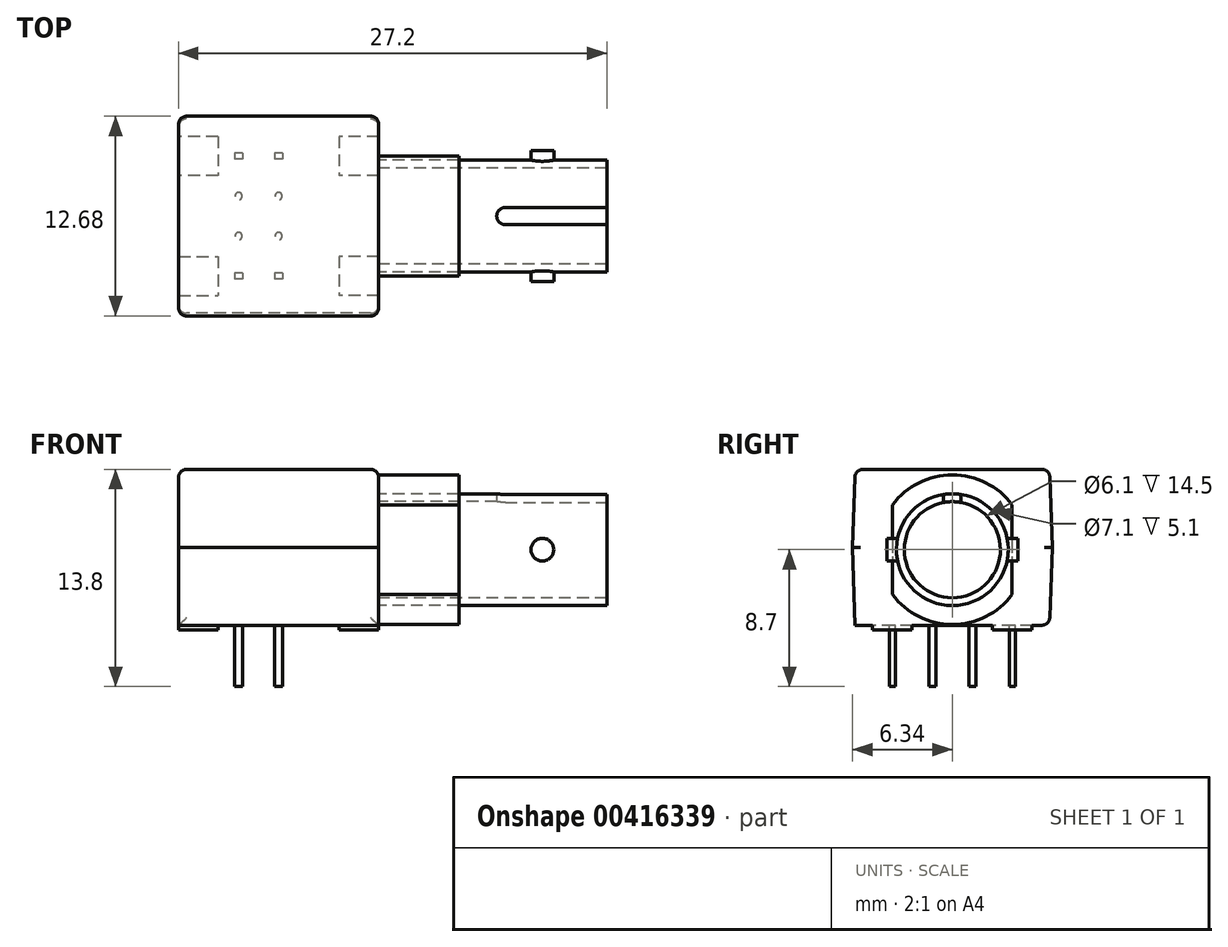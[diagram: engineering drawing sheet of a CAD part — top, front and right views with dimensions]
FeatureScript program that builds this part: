
annotation { "Feature Type Name" : "Feature", "Feature Type Description" : "" }
export const myFeature = defineFeature(function(context is Context, id is Id, definition is map)
    precondition{}
    {
        {
            var Q0;
            Q0=qCreatedBy(makeId("Top.planeOp"),FACE);
            var sketch = newSketch(context, id + "F0", { "sketchPlane" : qUnion([Q0])});
            skLineSegment(sketch, "E0.bottom", {"start": v(-6.35, 6.35) * mm, "end": v(6.35, 6.35) * mm});
            skLineSegment(sketch, "E0.top", {"start": v(-6.35, -6.35) * mm, "end": v(6.35, -6.35) * mm});
            skLineSegment(sketch, "E0.left", {"start": v(-6.35, 6.35) * mm, "end": v(-6.35, -6.35) * mm});
            skLineSegment(sketch, "E0.right", {"start": v(6.35, 6.35) * mm, "end": v(6.35, -6.35) * mm});
            skPoint(sketch, "E0.middle", {"position": v(0, 0) * mm});
            skSolve(sketch);
        }
        {
            var Q0;
            Q0=makeQuery(id+"F0.imprint","IMPRINT",FACE,{"disambiguationData":[TD([[makeQuery(id+"F0.imprint","IMPRINT",EDGE,{"derivedFrom":sQuery(id+"F0.wireOp",EDGE,"E0.bottom")}),-1.0]])]});
            extrude(context, id + "F1", {"entities" : qUnion([Q0]), "depth" : 5.1 * mm, "hasSecondDirection" : true, "secondDirectionOppositeDirection" : true, "secondDirectionDepth" : 4.8 * mm});
        }
        {
            var Q0;
            Q0=makeQuery(id+"F1.opExtrude","CAP_EDGE",EDGE,{"disambiguationData":[OSD([sQuery(id+"F0.wireOp",EDGE,"E0.bottom")])],"isStart":false});
            var Q1;
            Q1=makeQuery(id+"F1.opExtrude","CAP_EDGE",EDGE,{"disambiguationData":[OSD([sQuery(id+"F0.wireOp",EDGE,"E0.top")])],"isStart":false});
            var Q2;
            Q2=makeQuery(id+"F1.opExtrude","CAP_EDGE",EDGE,{"disambiguationData":[OSD([sQuery(id+"F0.wireOp",EDGE,"E0.top")])],"isStart":true});
            var Q3;
            Q3=makeQuery(id+"F1.opExtrude","CAP_EDGE",EDGE,{"disambiguationData":[OSD([sQuery(id+"F0.wireOp",EDGE,"E0.bottom")])],"isStart":true});
            chamfer(context, id + "F2", {"entities" : qUnion([Q0, Q1, Q2, Q3]), "chamferType" : ChamferType.OFFSET_ANGLE, "width" : 5.1 * mm, "oppositeDirection" : false, "angle" : 2 * degree, "tangentPropagation" : true});
        }
        {
            var Q0;
            Q0=makeQuery(id+"F1.opExtrude","SWEPT_FACE",FACE,{"disambiguationData":[OSD([sQuery(id+"F0.wireOp",EDGE,"E0.right")])]});
            var sketch = newSketch(context, id + "F3", { "sketchPlane" : qUnion([Q0])});
            skCircle(sketch, "E1", {"center": v(0, 0) * mm, "radius": 4.75 * mm});
            skCircle(sketch, "E2", {"center": v(0, 0) * mm, "radius": 3.55 * mm});
            skCircle(sketch, "E3", {"center": v(0, 0) * mm, "radius": 3.05 * mm});
            skSolve(sketch);
        }
        {
            var Q0;
            Q0=makeQuery(id+"F3.imprint","IMPRINT",FACE,{"disambiguationData":[TD([[makeQuery(id+"F3.imprint","IMPRINT",EDGE,{"derivedFrom":sQuery(id+"F3.wireOp",EDGE,"E1")}),1.0]])]});
            extrude(context, id + "F4", {"entities" : qUnion([Q0]), "depth" : 5.1 * mm});
        }
        {
            var Q0;
            Q0=makeQuery(id+"F3.imprint","IMPRINT",FACE,{"disambiguationData":[TD([[makeQuery(id+"F3.imprint","IMPRINT",EDGE,{"derivedFrom":sQuery(id+"F3.wireOp",EDGE,"E2")}),1.0]])]});
            extrude(context, id + "F5", {"entities" : qUnion([Q0]), "depth" : 14.5 * mm});
        }
        {
            var Q0;
            Q0=makeQuery(id+"F5.opExtrude","CAP_FACE",FACE,{"disambiguationData":[OSD([sQuery(id+"F3.wireOp",EDGE,"E2"),sQuery(id+"F3.wireOp",EDGE,"E3")])],"isStart":false});
            var sketch = newSketch(context, id + "F6", { "sketchPlane" : qUnion([Q0])});
            skSolve(sketch);
        }
        {
            var Q0;
            Q0=makeQuery(id+"F6.imprint","IMPRINT",FACE,{"disambiguationData":[TD([[makeQuery(id+"F6.imprint","IMPRINT",EDGE,{"derivedFrom":makeQuery(id+"F5.opExtrude","CAP_EDGE",EDGE,{"disambiguationData":[OSD([sQuery(id+"F3.wireOp",EDGE,"E2")])],"isStart":false})}),1.0]])]});
            var sketch = newSketch(context, id + "F7", { "sketchPlane" : qUnion([Q0])});
            skLineSegment(sketch, "E4", {"start": v(0.55, 3.5) * mm, "end": v(0.55, 3) * mm});
            skLineSegment(sketch, "E5", {"start": v(-0.55, 3) * mm, "end": v(-0.55, 3.5) * mm});
            skArc(sketch, "E6", {"start": v(0.55, 3.5) * mm, "mid": v(0, 3.55) * mm, "end": v(-0.55, 3.5) * mm});
            skArc(sketch, "E7", {"start": v(0.55, 3) * mm, "mid": v(0, 3.05) * mm, "end": v(-0.55, 3) * mm});
            skSolve(sketch);
        }
        {
            var Q0;
            Q0=makeQuery(id+"F7.imprint","IMPRINT",FACE,{"disambiguationData":[TD([[makeQuery(id+"F7.imprint","IMPRINT",EDGE,{"derivedFrom":sQuery(id+"F7.wireOp",EDGE,"E4")}),-1.0]])]});
            extrude(context, id + "F8", {"entities" : qUnion([Q0]), "operationType" : NewBodyOperationType.REMOVE, "oppositeDirection" : true, "depth" : 7 * mm});
        }
        {
            var Q0;
            Q0=makeQuery(id+"F8.boolean.opBoolean","COPY",EDGE,{"derivedFrom":makeQuery(id+"F8.opExtrude","CAP_EDGE",EDGE,{"disambiguationData":[OSD([sQuery(id+"F7.wireOp",EDGE,"E5")])],"isStart":false})});
            var Q1;
            Q1=makeQuery(id+"F8.boolean.opBoolean","COPY",EDGE,{"derivedFrom":makeQuery(id+"F8.opExtrude","CAP_EDGE",EDGE,{"disambiguationData":[OSD([sQuery(id+"F7.wireOp",EDGE,"E4")])],"isStart":false})});
            fillet(context, id + "F9", {"entities" : qUnion([Q0, Q1]), "radius" : 0.55 * mm, "tangentPropagation" : true, "allowEdgeOverflow" : false});
        }
        {
            var Q0;
            Q0=makeQuery(id+"F4.opExtrude","CAP_FACE",FACE,{"disambiguationData":[OSD([sQuery(id+"F3.wireOp",EDGE,"E1"),sQuery(id+"F3.wireOp",EDGE,"E2")])],"isStart":false});
            var sketch = newSketch(context, id + "F10", { "sketchPlane" : qUnion([Q0])});
            skLineSegment(sketch, "E8", {"start": v(3.8, 2.85) * mm, "end": v(3.8, -2.85) * mm});
            skLineSegment(sketch, "E9", {"start": v(-3.8, 2.85) * mm, "end": v(-3.8, -2.85) * mm});
            skSolve(sketch);
        }
        {
            var Q0;
            {var subQ0=sQuery(id+"F10.wireOp",EDGE,"E8");Q0=makeQuery(id+"F10.imprint","IMPRINT",FACE,{"disambiguationData":[TD([[makeQuery(id+"F10.imprint","IMPRINT",EDGE,{"derivedFrom":subQ0}),1.0]])]});}
            extrude(context, id + "F11", {"entities" : qUnion([Q0]), "operationType" : NewBodyOperationType.REMOVE, "oppositeDirection" : true, "depth" : 5.1 * mm});
        }
        {
            var Q0;
            {var subQ0=sQuery(id+"F10.wireOp",EDGE,"E9");Q0=makeQuery(id+"F10.imprint","IMPRINT",FACE,{"disambiguationData":[TD([[makeQuery(id+"F10.imprint","IMPRINT",EDGE,{"derivedFrom":subQ0}),-1.0]])]});}
            extrude(context, id + "F12", {"entities" : qUnion([Q0]), "operationType" : NewBodyOperationType.REMOVE, "oppositeDirection" : true, "depth" : 5.1 * mm});
        }
        {
            var Q0;
            Q0=makeQuery(id+"F1.opExtrude","CAP_FACE",FACE,{"disambiguationData":[OSD([sQuery(id+"F0.wireOp",EDGE,"E0.bottom"),sQuery(id+"F0.wireOp",EDGE,"E0.top"),sQuery(id+"F0.wireOp",EDGE,"E0.left"),sQuery(id+"F0.wireOp",EDGE,"E0.right")])],"isStart":true});
            var sketch = newSketch(context, id + "F13", { "sketchPlane" : qUnion([Q0])});
            skLineSegment(sketch, "E10.bottom", {"start": v(0.26, 3.62) * mm, "end": v(-0.26, 3.62) * mm});
            skLineSegment(sketch, "E10.top", {"start": v(0.26, 4) * mm, "end": v(-0.26, 4) * mm});
            skLineSegment(sketch, "E10.left", {"start": v(0.26, 3.62) * mm, "end": v(0.25, 4) * mm});
            skLineSegment(sketch, "E10.right", {"start": v(-0.25, 3.62) * mm, "end": v(-0.26, 4) * mm});
            skPoint(sketch, "E10.middle", {"position": v(0, 3.81) * mm});
            skLineSegment(sketch, "E11.bottom", {"start": v(-2.29, -4) * mm, "end": v(-2.8, -4) * mm});
            skLineSegment(sketch, "E11.top", {"start": v(-2.29, -3.62) * mm, "end": v(-2.8, -3.62) * mm});
            skLineSegment(sketch, "E11.left", {"start": v(-2.29, -4) * mm, "end": v(-2.29, -3.62) * mm});
            skLineSegment(sketch, "E11.right", {"start": v(-2.8, -4) * mm, "end": v(-2.8, -3.62) * mm});
            skPoint(sketch, "E11.middle", {"position": v(-2.54, -3.81) * mm});
            skLineSegment(sketch, "E12.bottom", {"start": v(0.25, -4) * mm, "end": v(-0.26, -4) * mm});
            skLineSegment(sketch, "E12.top", {"start": v(0.25, -3.62) * mm, "end": v(-0.26, -3.62) * mm});
            skLineSegment(sketch, "E12.left", {"start": v(0.25, -4) * mm, "end": v(0.25, -3.62) * mm});
            skLineSegment(sketch, "E12.right", {"start": v(-0.26, -4) * mm, "end": v(-0.26, -3.62) * mm});
            skPoint(sketch, "E12.middle", {"position": v(0, -3.81) * mm});
            skLineSegment(sketch, "E13.bottom", {"start": v(-2.29, 3.62) * mm, "end": v(-2.8, 3.62) * mm});
            skLineSegment(sketch, "E13.top", {"start": v(-2.29, 4) * mm, "end": v(-2.8, 4) * mm});
            skLineSegment(sketch, "E13.left", {"start": v(-2.29, 3.62) * mm, "end": v(-2.29, 4) * mm});
            skLineSegment(sketch, "E13.right", {"start": v(-2.8, 3.62) * mm, "end": v(-2.8, 4) * mm});
            skPoint(sketch, "E13.middle", {"position": v(-2.54, 3.81) * mm});
            skPoint(sketch, "E14", {"position": v(-2.29, -3.81) * mm});
            skCircle(sketch, "E15", {"center": v(-2.54, 1.27) * mm, "radius": 0.23 * mm});
            skCircle(sketch, "E16", {"center": v(-2.54, -1.27) * mm, "radius": 0.23 * mm});
            skCircle(sketch, "E17", {"center": v(0, 1.27) * mm, "radius": 0.23 * mm});
            skCircle(sketch, "E18", {"center": v(0, -1.27) * mm, "radius": 0.23 * mm});
            skLineSegment(sketch, "E19.bottom", {"start": v(6.35, 2.56) * mm, "end": v(3.85, 2.56) * mm});
            skLineSegment(sketch, "E19.top", {"start": v(6.35, 5.06) * mm, "end": v(3.85, 5.06) * mm});
            skLineSegment(sketch, "E19.left", {"start": v(6.35, 2.56) * mm, "end": v(6.35, 5.06) * mm});
            skLineSegment(sketch, "E19.right", {"start": v(3.85, 2.56) * mm, "end": v(3.85, 5.06) * mm});
            skPoint(sketch, "E19.middle", {"position": v(5.1, 3.8) * mm});
            skLineSegment(sketch, "E20.bottom", {"start": v(6.35, -5.06) * mm, "end": v(3.85, -5.06) * mm});
            skLineSegment(sketch, "E20.top", {"start": v(6.35, -2.56) * mm, "end": v(3.85, -2.56) * mm});
            skLineSegment(sketch, "E20.left", {"start": v(6.35, -5.06) * mm, "end": v(6.35, -2.56) * mm});
            skLineSegment(sketch, "E20.right", {"start": v(3.85, -5.06) * mm, "end": v(3.85, -2.56) * mm});
            skPoint(sketch, "E20.middle", {"position": v(5.1, -3.8) * mm});
            skLineSegment(sketch, "E21.bottom", {"start": v(-6.35, 2.56) * mm, "end": v(-3.85, 2.56) * mm});
            skLineSegment(sketch, "E21.top", {"start": v(-6.35, 5.06) * mm, "end": v(-3.85, 5.06) * mm});
            skLineSegment(sketch, "E21.left", {"start": v(-6.35, 2.56) * mm, "end": v(-6.35, 5.06) * mm});
            skLineSegment(sketch, "E21.right", {"start": v(-3.85, 2.56) * mm, "end": v(-3.85, 5.06) * mm});
            skPoint(sketch, "E21.middle", {"position": v(-5.1, 3.81) * mm});
            skLineSegment(sketch, "E22.bottom", {"start": v(-3.85, -5.06) * mm, "end": v(-6.35, -5.06) * mm});
            skLineSegment(sketch, "E22.top", {"start": v(-3.85, -2.56) * mm, "end": v(-6.35, -2.56) * mm});
            skLineSegment(sketch, "E22.left", {"start": v(-3.85, -5.06) * mm, "end": v(-3.85, -2.56) * mm});
            skLineSegment(sketch, "E22.right", {"start": v(-6.35, -5.06) * mm, "end": v(-6.35, -2.56) * mm});
            skPoint(sketch, "E22.middle", {"position": v(-5.1, -3.8) * mm});
            skSolve(sketch);
        }
        {
            var Q0;
            Q0=makeQuery(id+"F13.imprint","IMPRINT",FACE,{"disambiguationData":[TD([[makeQuery(id+"F13.imprint","IMPRINT",EDGE,{"derivedFrom":sQuery(id+"F13.wireOp",EDGE,"E15")}),1.0]])]});
            var Q1;
            Q1=makeQuery(id+"F13.imprint","IMPRINT",FACE,{"disambiguationData":[TD([[makeQuery(id+"F13.imprint","IMPRINT",EDGE,{"derivedFrom":sQuery(id+"F13.wireOp",EDGE,"E17")}),1.0]])]});
            var Q2;
            Q2=makeQuery(id+"F13.imprint","IMPRINT",FACE,{"disambiguationData":[TD([[makeQuery(id+"F13.imprint","IMPRINT",EDGE,{"derivedFrom":sQuery(id+"F13.wireOp",EDGE,"E16")}),1.0]])]});
            var Q3;
            Q3=makeQuery(id+"F13.imprint","IMPRINT",FACE,{"disambiguationData":[TD([[makeQuery(id+"F13.imprint","IMPRINT",EDGE,{"derivedFrom":sQuery(id+"F13.wireOp",EDGE,"E18")}),1.0]])]});
            var Q4;
            Q4=makeQuery(id+"F13.imprint","IMPRINT",FACE,{"disambiguationData":[TD([[makeQuery(id+"F13.imprint","IMPRINT",EDGE,{"derivedFrom":sQuery(id+"F13.wireOp",EDGE,"E12.bottom")}),-1.0]])]});
            var Q5;
            Q5=makeQuery(id+"F13.imprint","IMPRINT",FACE,{"disambiguationData":[TD([[makeQuery(id+"F13.imprint","IMPRINT",EDGE,{"derivedFrom":sQuery(id+"F13.wireOp",EDGE,"E11.bottom")}),-1.0]])]});
            var Q6;
            Q6=makeQuery(id+"F13.imprint","IMPRINT",FACE,{"disambiguationData":[TD([[makeQuery(id+"F13.imprint","IMPRINT",EDGE,{"derivedFrom":sQuery(id+"F13.wireOp",EDGE,"E10.bottom")}),-1.0]])]});
            var Q7;
            Q7=makeQuery(id+"F13.imprint","IMPRINT",FACE,{"disambiguationData":[TD([[makeQuery(id+"F13.imprint","IMPRINT",EDGE,{"derivedFrom":sQuery(id+"F13.wireOp",EDGE,"E13.bottom")}),-1.0]])]});
            extrude(context, id + "F14", {"entities" : qUnion([Q0, Q1, Q2, Q3, Q4, Q5, Q6, Q7]), "depth" : 3.9 * mm});
        }
        {
            var Q0;
            Q0=makeQuery(id+"F13.imprint","IMPRINT",FACE,{"disambiguationData":[TD([[makeQuery(id+"F13.imprint","IMPRINT",EDGE,{"derivedFrom":sQuery(id+"F13.wireOp",EDGE,"E21.bottom")}),1.0]])]});
            var Q1;
            Q1=makeQuery(id+"F13.imprint","IMPRINT",FACE,{"disambiguationData":[TD([[makeQuery(id+"F13.imprint","IMPRINT",EDGE,{"derivedFrom":sQuery(id+"F13.wireOp",EDGE,"E22.bottom")}),-1.0]])]});
            var Q2;
            Q2=makeQuery(id+"F13.imprint","IMPRINT",FACE,{"disambiguationData":[TD([[makeQuery(id+"F13.imprint","IMPRINT",EDGE,{"derivedFrom":sQuery(id+"F13.wireOp",EDGE,"E20.bottom")}),-1.0]])]});
            var Q3;
            Q3=makeQuery(id+"F13.imprint","IMPRINT",FACE,{"disambiguationData":[TD([[makeQuery(id+"F13.imprint","IMPRINT",EDGE,{"derivedFrom":sQuery(id+"F13.wireOp",EDGE,"E19.bottom")}),-1.0]])]});
            extrude(context, id + "F15", {"entities" : qUnion([Q0, Q1, Q2, Q3]), "operationType" : NewBodyOperationType.ADD, "depth" : 0.3 * mm});
        }
        {
            var Q0;
            {var subQ0=sQuery(id+"F0.wireOp",EDGE,"E0.top");Q0=makeQuery(id+"F2.opChamfer","BLEND_EDGE",EDGE,{"blendedFrom":[makeQuery(id+"F1.opExtrude","CAP_EDGE",EDGE,{"disambiguationData":[OSD([subQ0])],"isStart":false}),makeQuery(id+"F1.opExtrude","CAP_FACE",FACE,{"disambiguationData":[OSD([sQuery(id+"F0.wireOp",EDGE,"E0.bottom"),subQ0,sQuery(id+"F0.wireOp",EDGE,"E0.left"),sQuery(id+"F0.wireOp",EDGE,"E0.right")])],"isStart":false})],"blendedInto":[makeQuery(id+"F1.opExtrude","CAP_FACE",FACE,{"disambiguationData":[OSD([sQuery(id+"F0.wireOp",EDGE,"E0.bottom"),subQ0,sQuery(id+"F0.wireOp",EDGE,"E0.left"),sQuery(id+"F0.wireOp",EDGE,"E0.right")])],"isStart":false})]});}
            var Q1;
            Q1=makeQuery(id+"F1.opExtrude","CAP_EDGE",EDGE,{"disambiguationData":[OSD([sQuery(id+"F0.wireOp",EDGE,"E0.left")])],"isStart":false});
            var Q2;
            {var subQ0=sQuery(id+"F0.wireOp",EDGE,"E0.bottom");Q2=makeQuery(id+"F2.opChamfer","BLEND_EDGE",EDGE,{"blendedFrom":[makeQuery(id+"F1.opExtrude","CAP_EDGE",EDGE,{"disambiguationData":[OSD([subQ0])],"isStart":false}),makeQuery(id+"F1.opExtrude","CAP_FACE",FACE,{"disambiguationData":[OSD([subQ0,sQuery(id+"F0.wireOp",EDGE,"E0.top"),sQuery(id+"F0.wireOp",EDGE,"E0.left"),sQuery(id+"F0.wireOp",EDGE,"E0.right")])],"isStart":false})],"blendedInto":[makeQuery(id+"F1.opExtrude","CAP_FACE",FACE,{"disambiguationData":[OSD([subQ0,sQuery(id+"F0.wireOp",EDGE,"E0.top"),sQuery(id+"F0.wireOp",EDGE,"E0.left"),sQuery(id+"F0.wireOp",EDGE,"E0.right")])],"isStart":false})]});}
            var Q3;
            Q3=makeQuery(id+"F1.opExtrude","CAP_EDGE",EDGE,{"disambiguationData":[OSD([sQuery(id+"F0.wireOp",EDGE,"E0.right")])],"isStart":false});
            var Q4;
            Q4=makeQuery(id+"F2.opChamfer","BLEND_EDGE",EDGE,{"blendedFrom":[makeQuery(id+"F1.opExtrude","CAP_EDGE",EDGE,{"disambiguationData":[OSD([sQuery(id+"F0.wireOp",EDGE,"E0.top")])],"isStart":false}),makeQuery(id+"F1.opExtrude","SWEPT_FACE",FACE,{"disambiguationData":[OSD([sQuery(id+"F0.wireOp",EDGE,"E0.right")])]})],"blendedInto":[makeQuery(id+"F1.opExtrude","SWEPT_FACE",FACE,{"disambiguationData":[OSD([sQuery(id+"F0.wireOp",EDGE,"E0.right")])]})]});
            var Q5;
            Q5=makeQuery(id+"F2.opChamfer","BLEND_EDGE",EDGE,{"blendedFrom":[makeQuery(id+"F1.opExtrude","CAP_EDGE",EDGE,{"disambiguationData":[OSD([sQuery(id+"F0.wireOp",EDGE,"E0.top")])],"isStart":true}),makeQuery(id+"F1.opExtrude","SWEPT_FACE",FACE,{"disambiguationData":[OSD([sQuery(id+"F0.wireOp",EDGE,"E0.right")])]})],"blendedInto":[makeQuery(id+"F1.opExtrude","SWEPT_FACE",FACE,{"disambiguationData":[OSD([sQuery(id+"F0.wireOp",EDGE,"E0.right")])]})]});
            var Q6;
            Q6=makeQuery(id+"F2.opChamfer","BLEND_EDGE",EDGE,{"blendedFrom":[makeQuery(id+"F1.opExtrude","CAP_EDGE",EDGE,{"disambiguationData":[OSD([sQuery(id+"F0.wireOp",EDGE,"E0.top")])],"isStart":false}),makeQuery(id+"F1.opExtrude","SWEPT_FACE",FACE,{"disambiguationData":[OSD([sQuery(id+"F0.wireOp",EDGE,"E0.left")])]})],"blendedInto":[makeQuery(id+"F1.opExtrude","SWEPT_FACE",FACE,{"disambiguationData":[OSD([sQuery(id+"F0.wireOp",EDGE,"E0.left")])]})]});
            var Q7;
            Q7=makeQuery(id+"F2.opChamfer","BLEND_EDGE",EDGE,{"blendedFrom":[makeQuery(id+"F1.opExtrude","CAP_EDGE",EDGE,{"disambiguationData":[OSD([sQuery(id+"F0.wireOp",EDGE,"E0.top")])],"isStart":true}),makeQuery(id+"F1.opExtrude","SWEPT_FACE",FACE,{"disambiguationData":[OSD([sQuery(id+"F0.wireOp",EDGE,"E0.left")])]})],"blendedInto":[makeQuery(id+"F1.opExtrude","SWEPT_FACE",FACE,{"disambiguationData":[OSD([sQuery(id+"F0.wireOp",EDGE,"E0.left")])]})]});
            var Q8;
            Q8=makeQuery(id+"F2.opChamfer","BLEND_EDGE",EDGE,{"blendedFrom":[makeQuery(id+"F1.opExtrude","CAP_EDGE",EDGE,{"disambiguationData":[OSD([sQuery(id+"F0.wireOp",EDGE,"E0.bottom")])],"isStart":false}),makeQuery(id+"F1.opExtrude","SWEPT_FACE",FACE,{"disambiguationData":[OSD([sQuery(id+"F0.wireOp",EDGE,"E0.left")])]})],"blendedInto":[makeQuery(id+"F1.opExtrude","SWEPT_FACE",FACE,{"disambiguationData":[OSD([sQuery(id+"F0.wireOp",EDGE,"E0.left")])]})]});
            var Q9;
            Q9=makeQuery(id+"F2.opChamfer","BLEND_EDGE",EDGE,{"blendedFrom":[makeQuery(id+"F1.opExtrude","CAP_EDGE",EDGE,{"disambiguationData":[OSD([sQuery(id+"F0.wireOp",EDGE,"E0.bottom")])],"isStart":true}),makeQuery(id+"F1.opExtrude","SWEPT_FACE",FACE,{"disambiguationData":[OSD([sQuery(id+"F0.wireOp",EDGE,"E0.left")])]})],"blendedInto":[makeQuery(id+"F1.opExtrude","SWEPT_FACE",FACE,{"disambiguationData":[OSD([sQuery(id+"F0.wireOp",EDGE,"E0.left")])]})]});
            var Q10;
            {var subQ0=sQuery(id+"F0.wireOp",EDGE,"E0.bottom");Q10=makeQuery(id+"F2.opChamfer","BLEND_EDGE",EDGE,{"blendedFrom":[makeQuery(id+"F1.opExtrude","CAP_EDGE",EDGE,{"disambiguationData":[OSD([subQ0])],"isStart":true}),makeQuery(id+"F1.opExtrude","CAP_FACE",FACE,{"disambiguationData":[OSD([subQ0,sQuery(id+"F0.wireOp",EDGE,"E0.top"),sQuery(id+"F0.wireOp",EDGE,"E0.left"),sQuery(id+"F0.wireOp",EDGE,"E0.right")])],"isStart":true})],"blendedInto":[makeQuery(id+"F1.opExtrude","CAP_FACE",FACE,{"disambiguationData":[OSD([subQ0,sQuery(id+"F0.wireOp",EDGE,"E0.top"),sQuery(id+"F0.wireOp",EDGE,"E0.left"),sQuery(id+"F0.wireOp",EDGE,"E0.right")])],"isStart":true})]});}
            var Q11;
            Q11=makeQuery(id+"F2.opChamfer","BLEND_EDGE",EDGE,{"blendedFrom":[makeQuery(id+"F1.opExtrude","CAP_EDGE",EDGE,{"disambiguationData":[OSD([sQuery(id+"F0.wireOp",EDGE,"E0.bottom")])],"isStart":true}),makeQuery(id+"F1.opExtrude","SWEPT_FACE",FACE,{"disambiguationData":[OSD([sQuery(id+"F0.wireOp",EDGE,"E0.right")])]})],"blendedInto":[makeQuery(id+"F1.opExtrude","SWEPT_FACE",FACE,{"disambiguationData":[OSD([sQuery(id+"F0.wireOp",EDGE,"E0.right")])]})]});
            var Q12;
            Q12=makeQuery(id+"F2.opChamfer","BLEND_EDGE",EDGE,{"blendedFrom":[makeQuery(id+"F1.opExtrude","CAP_EDGE",EDGE,{"disambiguationData":[OSD([sQuery(id+"F0.wireOp",EDGE,"E0.bottom")])],"isStart":false}),makeQuery(id+"F1.opExtrude","SWEPT_FACE",FACE,{"disambiguationData":[OSD([sQuery(id+"F0.wireOp",EDGE,"E0.right")])]})],"blendedInto":[makeQuery(id+"F1.opExtrude","SWEPT_FACE",FACE,{"disambiguationData":[OSD([sQuery(id+"F0.wireOp",EDGE,"E0.right")])]})]});
            fillet(context, id + "F16", {"entities" : qUnion([Q0, Q1, Q2, Q3, Q4, Q5, Q6, Q7, Q8, Q9, Q10, Q11, Q12]), "radius" : 0.5 * mm, "tangentPropagation" : true, "allowEdgeOverflow" : false});
        }
        {
            var Q0;
            Q0=qCreatedBy(makeId("Front.planeOp"),FACE);
            cPlane(context, id + "F17", {"entities" : qUnion([Q0]), "cplaneType" : CPlaneType.OFFSET, "offset" : 3.1 * mm, "width" : 150 * mm, "height" : 150 * mm});
        }
        {
            var Q0;
            Q0=qCreatedBy(id+"F17.planeOp",FACE);
            var sketch = newSketch(context, id + "F18", { "sketchPlane" : qUnion([Q0])});
            skCircle(sketch, "E23", {"center": v(16.75, 0) * mm, "radius": 0.72 * mm});
            skSolve(sketch);
        }
        {
            var Q0;
            Q0 = qSketchRegion(id + "F18", true);
            var Q1;
            Q1=sQuery(id+"F18.wireOp",EDGE,"E23");
            extrude(context, id + "F19", {"entities" : qUnion([Q0]), "operationType" : NewBodyOperationType.ADD, "surfaceEntities" : qUnion([Q1]), "depth" : 1.05 * mm});
        }
        {
            var Q0;
            Q0=qCreatedBy(makeId("Front.planeOp"),FACE);
            cPlane(context, id + "F20", {"entities" : qUnion([Q0]), "cplaneType" : CPlaneType.OFFSET, "offset" : 3.1 * mm, "oppositeDirection" : true, "width" : 150 * mm, "height" : 150 * mm});
        }
        {
            var Q0;
            Q0=qCreatedBy(id+"F20.planeOp",FACE);
            var sketch = newSketch(context, id + "F21", { "sketchPlane" : qUnion([Q0])});
            skCircle(sketch, "E24", {"center": v(16.75, 0) * mm, "radius": 0.72 * mm});
            skSolve(sketch);
        }
        {
            var Q0;
            Q0=makeQuery(id+"F21.imprint","IMPRINT",FACE,{"disambiguationData":[TD([[makeQuery(id+"F21.imprint","IMPRINT",EDGE,{"derivedFrom":sQuery(id+"F21.wireOp",EDGE,"E24")}),1.0]])]});
            var Q1;
            Q1=sQuery(id+"F21.wireOp",EDGE,"E24");
            extrude(context, id + "F22", {"entities" : qUnion([Q0]), "operationType" : NewBodyOperationType.ADD, "surfaceEntities" : qUnion([Q1]), "oppositeDirection" : true, "depth" : 1.05 * mm});
        }
    });
